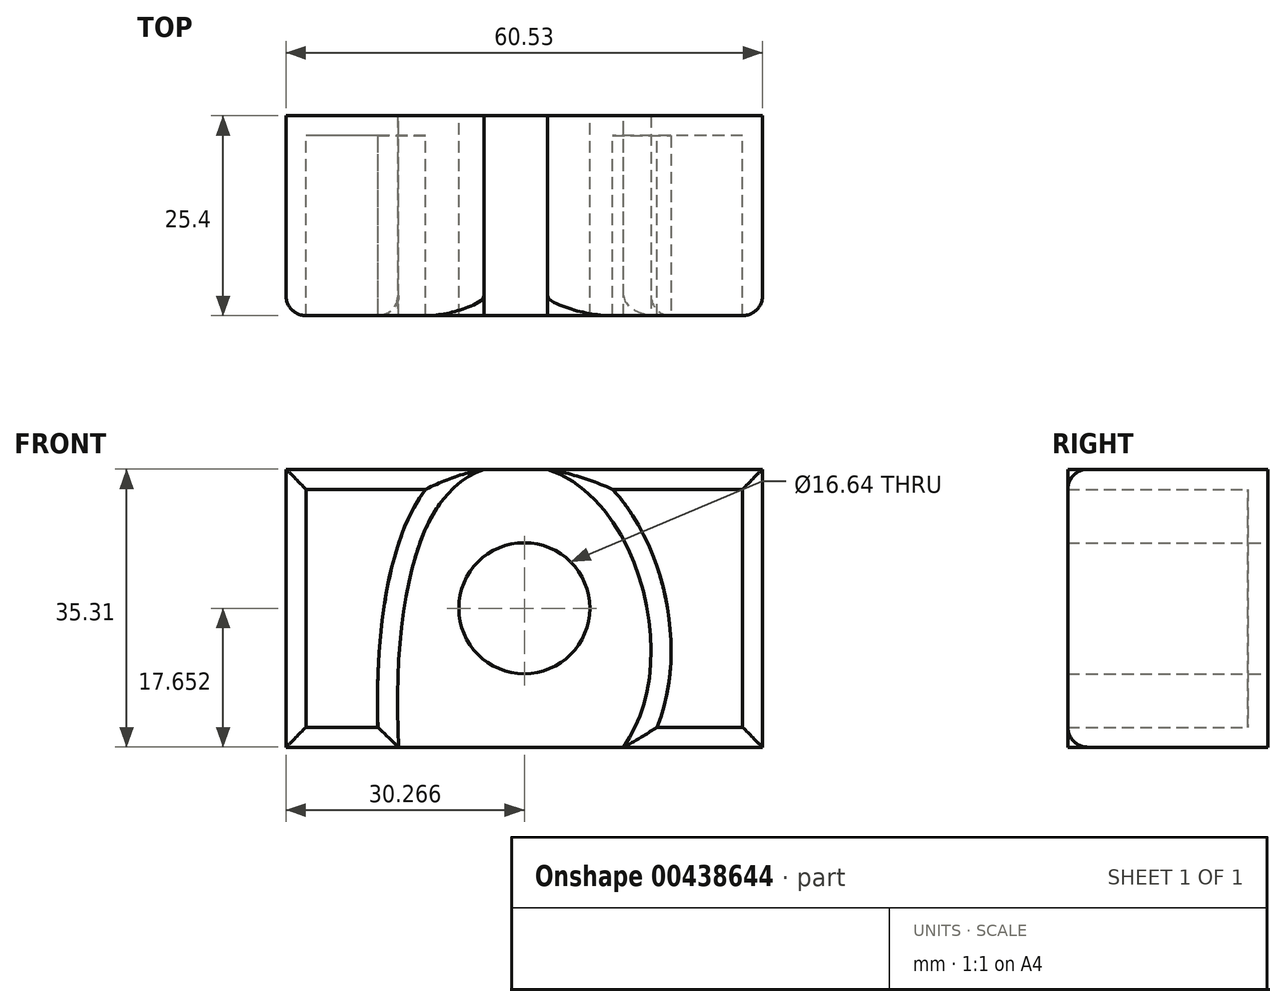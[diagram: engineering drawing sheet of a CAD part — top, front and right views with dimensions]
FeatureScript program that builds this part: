
annotation { "Feature Type Name" : "Feature", "Feature Type Description" : "" }
export const myFeature = defineFeature(function(context is Context, id is Id, definition is map)
    precondition{}
    {
        {
            var Q0;
            Q0=qCreatedBy(makeId("Front.planeOp"),FACE);
            var sketch = newSketch(context, id + "F0", { "sketchPlane" : qUnion([Q0])});
            skCircle(sketch, "E0", {"center": v(0, 0) * mm, "radius": 19 * mm});
            skFitSpline(sketch, "E1", {"points": [v(-11.89, -19.1) * mm, v(-18.37, -23.42) * mm, v(-38.2, -11.53) * mm, v(-41.43, 52.24) * mm, v(-25.58, 56.56) * mm, v(-15.13, 41.8) * mm, v(-15.85, 25.22) * mm, v(-21.26, 16.21) * mm, v(-23.42, 6.49) * mm, v(-25.22, -6.85) * mm, v(-11.89, -19.1) * mm]});
            skCircle(sketch, "E2", {"center": v(-30.26, 39.63) * mm, "radius": 8.32 * mm});
            skLineSegment(sketch, "E3.bottom", {"start": v(0, 57.29) * mm, "end": v(-60.53, 57.29) * mm});
            skLineSegment(sketch, "E3.top", {"start": v(0, 21.98) * mm, "end": v(-60.53, 21.98) * mm});
            skLineSegment(sketch, "E3.left", {"start": v(0, 57.29) * mm, "end": v(0, 21.98) * mm});
            skLineSegment(sketch, "E3.right", {"start": v(-60.53, 57.29) * mm, "end": v(-60.53, 21.98) * mm});
            skSolve(sketch);
        }
        {
            var Q0;
            Q0=makeQuery(id+"F0.imprint","IMPRINT",FACE,{"disambiguationData":[TD([[makeQuery(id+"F0.imprint","IMPRINT",EDGE,{"derivedFrom":sQuery(id+"F0.wireOp",EDGE,"E2")}),-1.0]])]});
            var Q1;
            {var subQ0=sQuery(id+"F0.wireOp",EDGE,"E3.top");var subQ1=sQuery(id+"F0.wireOp",EDGE,"E1");var subQ2=makeQuery(id+"F0.imprint","INTERSECT",VERTEX,{"disambiguationData":[OD(0.0)],"derivedFrom":[subQ1,subQ0]});Q1=makeQuery(id+"F0.imprint","IMPRINT",FACE,{"disambiguationData":[TD([[makeQuery(id+"F0.imprint","IMPRINT",EDGE,{"disambiguationData":[TD([[subQ2,1.0]])],"derivedFrom":subQ1}),-1.0]])]});}
            extrude(context, id + "F1", {"entities" : qUnion([Q0, Q1]), "depth" : 25.4 * mm});
        }
        {
            var Q0;
            {var subQ5=sQuery(id+"F0.wireOp",EDGE,"E3.right");Q0=makeQuery(id+"F0.imprint","IMPRINT",FACE,{"disambiguationData":[TD([[makeQuery(id+"F0.imprint","IMPRINT",EDGE,{"derivedFrom":subQ5}),1.0]])]});}
            var Q1;
            {var subQ5=sQuery(id+"F0.wireOp",EDGE,"E3.left");Q1=makeQuery(id+"F0.imprint","IMPRINT",FACE,{"disambiguationData":[TD([[makeQuery(id+"F0.imprint","IMPRINT",EDGE,{"derivedFrom":subQ5}),-1.0]])]});}
            extrude(context, id + "F2", {"entities" : qUnion([Q0, Q1]), "depth" : 25.4 * mm});
        }
        {
            var Q0;
            Q0=makeQuery(id+"F2.opExtrude","CAP_FACE",FACE,{"disambiguationData":[OSD([sQuery(id+"F0.wireOp",EDGE,"E1"),sQuery(id+"F0.wireOp",EDGE,"E3.bottom"),sQuery(id+"F0.wireOp",EDGE,"E3.top"),sQuery(id+"F0.wireOp",EDGE,"E3.right")])],"isStart":false});
            var Q1;
            Q1=makeQuery(id+"F2.opExtrude","CAP_FACE",FACE,{"disambiguationData":[OSD([sQuery(id+"F0.wireOp",EDGE,"E1"),sQuery(id+"F0.wireOp",EDGE,"E3.bottom"),sQuery(id+"F0.wireOp",EDGE,"E3.top"),sQuery(id+"F0.wireOp",EDGE,"E3.left")])],"isStart":false});
            fillet(context, id + "F3", {"entities" : qUnion([Q0, Q1]), "radius" : 2.54 * mm, "tangentPropagation" : true, "allowEdgeOverflow" : false});
        }
        {
            var Q0;
            Q0=makeQuery(id+"F2.opExtrude","CAP_FACE",FACE,{"disambiguationData":[OSD([sQuery(id+"F0.wireOp",EDGE,"E1"),sQuery(id+"F0.wireOp",EDGE,"E3.bottom"),sQuery(id+"F0.wireOp",EDGE,"E3.top"),sQuery(id+"F0.wireOp",EDGE,"E3.right")])],"isStart":false});
            var Q1;
            Q1=makeQuery(id+"F2.opExtrude","CAP_FACE",FACE,{"disambiguationData":[OSD([sQuery(id+"F0.wireOp",EDGE,"E1"),sQuery(id+"F0.wireOp",EDGE,"E3.bottom"),sQuery(id+"F0.wireOp",EDGE,"E3.top"),sQuery(id+"F0.wireOp",EDGE,"E3.left")])],"isStart":false});
            shell(context, id + "F4", {"entities" : qUnion([Q0, Q1]), "thickness" : 2.54 * mm});
        }
    });
